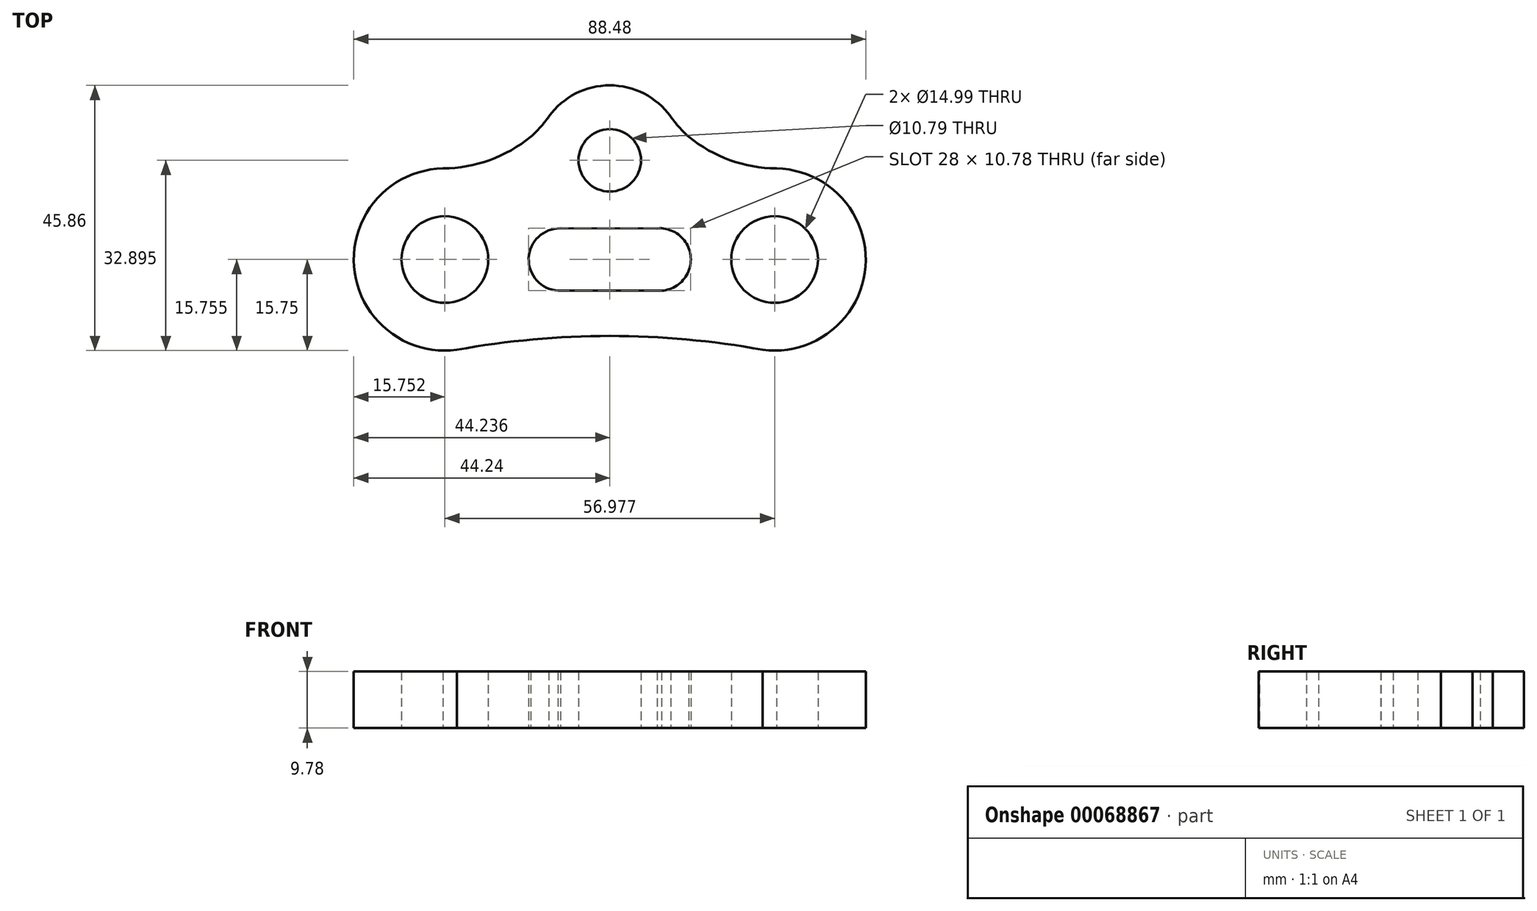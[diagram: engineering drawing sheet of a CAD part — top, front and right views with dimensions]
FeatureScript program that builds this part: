
annotation { "Feature Type Name" : "Feature", "Feature Type Description" : "" }
export const myFeature = defineFeature(function(context is Context, id is Id, definition is map)
    precondition{}
    {
        {
            var Q0;
            Q0=qCreatedBy(makeId("Top.planeOp"),FACE);
            var sketch = newSketch(context, id + "F0", { "sketchPlane" : qUnion([Q0])});
            skArc(sketch, "E0", {"start": v(-8.52, 5.4) * mm, "mid": v(-14, 0.21) * mm, "end": v(-8.95, -5.39) * mm});
            skArc(sketch, "E1.MirrorC", {"start": v(8.2, 5.38) * mm, "mid": v(14, 0.37) * mm, "end": v(8.95, -5.39) * mm});
            skPoint(sketch, "E2.center.orphan", {"position": v(-30.45, 0) * mm});
            skCircle(sketch, "E3", {"center": v(-28.49, 0) * mm, "radius": 7.5 * mm});
            skPoint(sketch, "E4.start.orphan", {"position": v(-19.72, 0) * mm});
            skLineSegment(sketch, "E5", {"start": v(-21, 0) * mm, "end": v(-14.01, 0) * mm});
            skCircle(sketch, "E6", {"center": v(0, 17.15) * mm, "radius": 5.4 * mm});
            skLineSegment(sketch, "E7", {"start": v(0, 11.75) * mm, "end": v(0, 4.76) * mm});
            skArc(sketch, "E8", {"start": v(-28.8, 15.74) * mm, "mid": v(-44.21, -0.84) * mm, "end": v(-27.13, -15.69) * mm});
            skLineSegment(sketch, "E9", {"start": v(-44.24, 0) * mm, "end": v(-35.98, 0) * mm});
            skArc(sketch, "E10", {"start": v(-28.8, 15.74) * mm, "mid": v(-20.76, 17.19) * mm, "end": v(-13.65, 21.23) * mm});
            skArc(sketch, "E11.MirrorCS", {"start": v(28.57, 15.75) * mm, "mid": v(44.2, -1.08) * mm, "end": v(26.41, -15.61) * mm});
            skCircle(sketch, "E12.MirrorC", {"center": v(28.49, 0) * mm, "radius": 7.5 * mm});
            skArc(sketch, "E13.MirrorCS", {"start": v(28.8, 15.74) * mm, "mid": v(20.76, 17.19) * mm, "end": v(13.65, 21.23) * mm});
            skPoint(sketch, "E14.orphan", {"position": v(-13.04, 3.08) * mm});
            skPoint(sketch, "E15.orphan", {"position": v(13.04, 3.08) * mm});
            skPoint(sketch, "E16.orphan", {"position": v(13.04, -3.08) * mm});
            skPoint(sketch, "E17.orphan", {"position": v(-13.04, -3.08) * mm});
            skArc(sketch, "E18.trimOffspring", {"start": v(10.52, 24.73) * mm, "mid": v(0, 30.11) * mm, "end": v(-10.52, 24.73) * mm});
            skLineSegment(sketch, "E19", {"start": v(-8.52, 5.4) * mm, "end": v(8.2, 5.38) * mm});
            skPoint(sketch, "E20.orphan", {"position": v(-5.42, 4.35) * mm});
            skPoint(sketch, "E21.orphan", {"position": v(5.42, 4.35) * mm});
            skLineSegment(sketch, "E22", {"start": v(-8.95, -5.39) * mm, "end": v(8.95, -5.39) * mm});
            skPoint(sketch, "E23.orphan", {"position": v(-5.42, -4.35) * mm});
            skPoint(sketch, "E24.MirrorCS.start.orphan", {"position": v(5.42, -4.35) * mm});
            skArc(sketch, "E25", {"start": v(-13.65, 21.23) * mm, "mid": v(-11.97, 22.88) * mm, "end": v(-10.52, 24.73) * mm});
            skPoint(sketch, "E26.orphan", {"position": v(-11.4, 23.32) * mm});
            skArc(sketch, "E27.MirrorCS", {"start": v(13.65, 21.23) * mm, "mid": v(11.97, 22.88) * mm, "end": v(10.52, 24.73) * mm});
            skPoint(sketch, "E28.orphan", {"position": v(11.4, 23.32) * mm});
            skArc(sketch, "E29", {"start": v(26.41, -15.61) * mm, "mid": v(13.26, -13.82) * mm, "end": v(0, -13.22) * mm});
            skPoint(sketch, "E30.orphan", {"position": v(27.13, -15.69) * mm});
            skPoint(sketch, "E31.end.orphan", {"position": v(-26.41, -15.61) * mm});
            skArc(sketch, "E32.MirrorCS", {"start": v(-26.41, -15.61) * mm, "mid": v(-13.26, -13.82) * mm, "end": v(0, -13.22) * mm});
            skArc(sketch, "E33.MirrorCS", {"start": v(-28.57, 15.75) * mm, "mid": v(-44.2, -1.08) * mm, "end": v(-26.41, -15.61) * mm});
            skSolve(sketch);
        }
        {
            var Q0;
            {var subQ0=sQuery(id+"F0.wireOp",EDGE,"E13.MirrorCS");var subQ1=sQuery(id+"F0.wireOp",EDGE,"E11.MirrorCS");var subQ2=makeQuery(id+"F0.imprint","INTERSECT",VERTEX,{"disambiguationData":[OD(0.0)],"derivedFrom":[subQ1,subQ0]});Q0=makeQuery(id+"F0.imprint","IMPRINT",FACE,{"disambiguationData":[TD([[makeQuery(id+"F0.imprint","IMPRINT",EDGE,{"disambiguationData":[TD([[subQ2,-1.0]])],"derivedFrom":subQ1}),-1.0]])]});}
            var Q1;
            Q1=makeQuery(id+"F0.imprint","IMPRINT",FACE,{"disambiguationData":[TD([[makeQuery(id+"F0.imprint","IMPRINT",EDGE,{"derivedFrom":sQuery(id+"F0.wireOp",EDGE,"E6")}),-1.0]])]});
            extrude(context, id + "F1", {"entities" : qUnion([Q0, Q1]), "depth" : 9.78 * mm});
        }
    });
